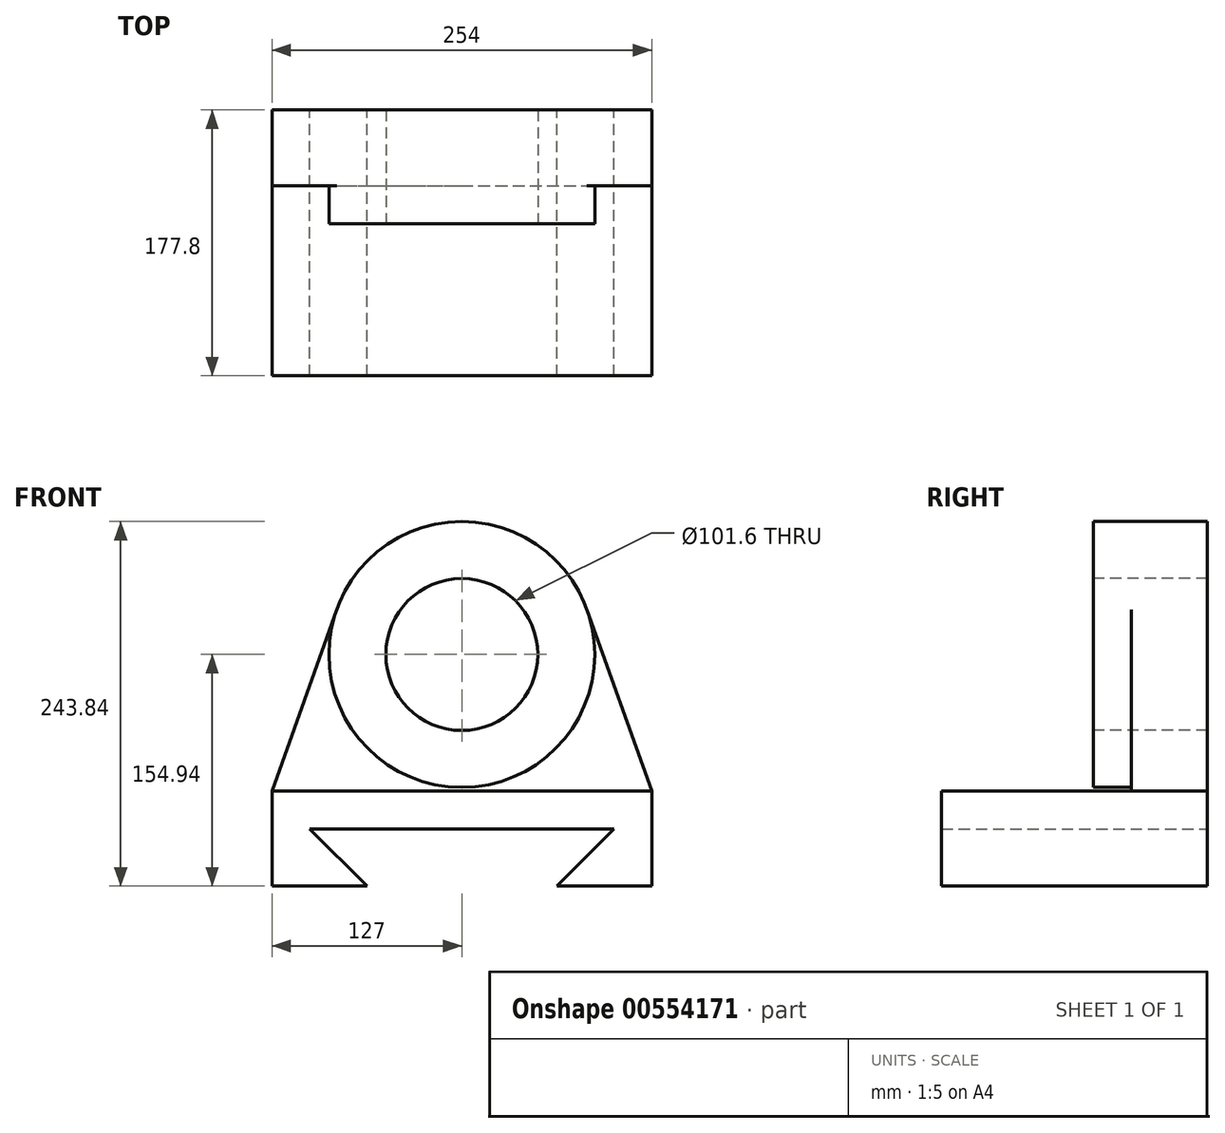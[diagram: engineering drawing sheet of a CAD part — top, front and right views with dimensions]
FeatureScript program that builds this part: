
annotation { "Feature Type Name" : "Feature", "Feature Type Description" : "" }
export const myFeature = defineFeature(function(context is Context, id is Id, definition is map)
    precondition{}
    {
        {
            var Q0;
            Q0=qCreatedBy(makeId("Front.planeOp"),FACE);
            var sketch = newSketch(context, id + "F0", { "sketchPlane" : qUnion([Q0])});
            skLineSegment(sketch, "E0", {"start": v(0, 0) * mm, "end": v(254, 0) * mm});
            skLineSegment(sketch, "E1", {"start": v(0, 0) * mm, "end": v(0, -63.5) * mm});
            skLineSegment(sketch, "E2", {"start": v(254, 0) * mm, "end": v(254, -63.5) * mm});
            skLineSegment(sketch, "E3", {"start": v(254, -63.5) * mm, "end": v(190.5, -63.5) * mm});
            skLineSegment(sketch, "E4", {"start": v(190.5, -63.5) * mm, "end": v(228.6, -25.4) * mm});
            skLineSegment(sketch, "E5", {"start": v(0, -63.5) * mm, "end": v(63.5, -63.5) * mm});
            skLineSegment(sketch, "E6", {"start": v(63.5, -63.5) * mm, "end": v(25.4, -25.4) * mm});
            skLineSegment(sketch, "E7", {"start": v(25.4, -25.4) * mm, "end": v(228.6, -25.4) * mm});
            skCircle(sketch, "E8", {"center": v(127, 91.44) * mm, "radius": 50.8 * mm});
            skCircle(sketch, "E9", {"center": v(127, 91.44) * mm, "radius": 88.9 * mm});
            skLineSegment(sketch, "E10", {"start": v(0, 0) * mm, "end": v(43.27, 121.3) * mm});
            skLineSegment(sketch, "E11", {"start": v(254, 0) * mm, "end": v(210.73, 121.3) * mm});
            skSolve(sketch);
        }
        {
            var Q0;
            Q0=makeQuery(id+"F0.imprint","IMPRINT",FACE,{"disambiguationData":[TD([[makeQuery(id+"F0.imprint","IMPRINT",EDGE,{"derivedFrom":sQuery(id+"F0.wireOp",EDGE,"E0")}),-1.0]])]});
            extrude(context, id + "F1", {"entities" : qUnion([Q0]), "depth" : 127 * mm, "offsetDistance" : 25.4 * mm});
        }
        {
            var Q0;
            Q0=makeQuery(id+"F0.imprint","IMPRINT",FACE,{"disambiguationData":[TD([[makeQuery(id+"F0.imprint","IMPRINT",EDGE,{"derivedFrom":sQuery(id+"F0.wireOp",EDGE,"E0")}),1.0]])]});
            var Q1;
            Q1=makeQuery(id+"F0.imprint","IMPRINT",FACE,{"disambiguationData":[TD([[makeQuery(id+"F0.imprint","IMPRINT",EDGE,{"derivedFrom":sQuery(id+"F0.wireOp",EDGE,"E0")}),-1.0]])]});
            var Q2;
            Q2=makeQuery(id+"F0.imprint","IMPRINT",FACE,{"disambiguationData":[TD([[makeQuery(id+"F0.imprint","IMPRINT",EDGE,{"derivedFrom":sQuery(id+"F0.wireOp",EDGE,"E8")}),-1.0]])]});
            extrude(context, id + "F2", {"entities" : qUnion([Q0, Q1, Q2]), "operationType" : NewBodyOperationType.ADD, "oppositeDirection" : true, "depth" : 50.8 * mm, "offsetDistance" : 25.4 * mm});
        }
        {
            var Q0;
            Q0=makeQuery(id+"F0.imprint","IMPRINT",FACE,{"disambiguationData":[TD([[makeQuery(id+"F0.imprint","IMPRINT",EDGE,{"derivedFrom":sQuery(id+"F0.wireOp",EDGE,"E8")}),-1.0]])]});
            extrude(context, id + "F3", {"entities" : qUnion([Q0]), "operationType" : NewBodyOperationType.ADD, "depth" : 25.4 * mm, "offsetDistance" : 25.4 * mm});
        }
    });
